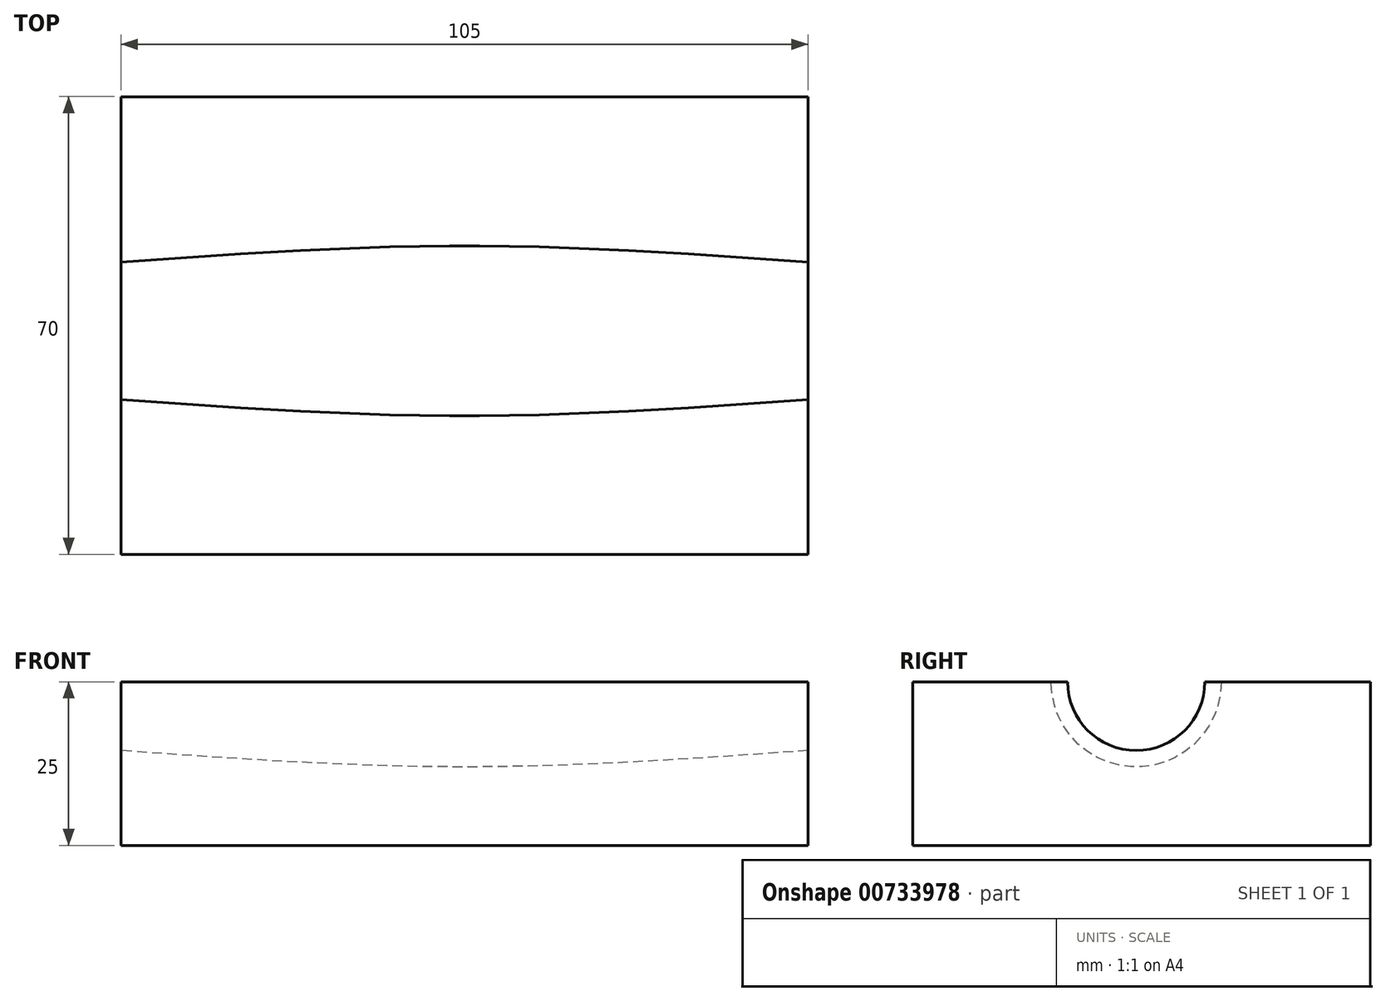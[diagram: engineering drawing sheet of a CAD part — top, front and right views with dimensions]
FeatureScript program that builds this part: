
annotation { "Feature Type Name" : "Feature", "Feature Type Description" : "" }
export const myFeature = defineFeature(function(context is Context, id is Id, definition is map)
    precondition{}
    {
        {
            var Q0;
            Q0=qCreatedBy(makeId("Front.planeOp"),FACE);
            var sketch = newSketch(context, id + "F0", { "sketchPlane" : qUnion([Q0])});
            skLineSegment(sketch, "E0", {"start": v(-90.68, 0) * mm, "end": v(100.6, 0) * mm, "construction": true});
            skLineSegment(sketch, "E1", {"start": v(-52.5, 0) * mm, "end": v(-52.5, 10.5) * mm});
            skLineSegment(sketch, "E2", {"start": v(52.5, 0) * mm, "end": v(52.5, 10.5) * mm});
            skLineSegment(sketch, "E3", {"start": v(-52.5, 0) * mm, "end": v(52.5, 0) * mm});
            skLineSegment(sketch, "E4", {"start": v(0, 0) * mm, "end": v(0, 13) * mm, "construction": true});
            skFitSpline(sketch, "E5", {"points": [v(-52.5, 10.5) * mm, v(0, 13) * mm, v(52.5, 10.5) * mm], "startDerivative": vector(105, 7.5) * mm, "endDerivative": vector(105, -7.5) * mm});
            skSolve(sketch);
        }
        {
            var Q0;
            Q0=qCreatedBy(makeId("Top.planeOp"),FACE);
            var sketch = newSketch(context, id + "F1", { "sketchPlane" : qUnion([Q0])});
            skLineSegment(sketch, "E6.bottom", {"start": v(-52.5, 35.82) * mm, "end": v(52.5, 35.82) * mm});
            skLineSegment(sketch, "E6.top", {"start": v(-52.5, -34.18) * mm, "end": v(52.5, -34.18) * mm});
            skLineSegment(sketch, "E6.left", {"start": v(-52.5, 35.82) * mm, "end": v(-52.5, -34.18) * mm});
            skLineSegment(sketch, "E6.right", {"start": v(52.5, 35.82) * mm, "end": v(52.5, -34.18) * mm});
            skSolve(sketch);
        }
        {
            var Q0;
            Q0 = qSketchRegion(id + "F1", true);
            extrude(context, id + "F2", {"entities" : qUnion([Q0]), "oppositeDirection" : true, "depth" : 25 * mm, "offsetDistance" : 25 * mm});
        }
        {
            var Q0;
            Q0=makeQuery(id+"F0.imprint","IMPRINT",FACE,{"disambiguationData":[TD([[makeQuery(id+"F0.imprint","IMPRINT",EDGE,{"derivedFrom":sQuery(id+"F0.wireOp",EDGE,"E1")}),-1.0]])]});
            var Q1;
            Q1=sQuery(id+"F0.wireOp",EDGE,"E0");
            revolve(context, id + "F3", {"operationType" : NewBodyOperationType.REMOVE, "surfaceOperationType" : NewSurfaceOperationType.NEW, "entities" : qUnion([Q0]), "axis" : qUnion([Q1]), "revolveType" : RevolveType.FULL, "oppositeDirection" : true});
        }
        {
            var Q0;
            Q0=makeQuery(id+"F2.opExtrude","SWEPT_BODY",BODY,{"disambiguationData":[OSD([sQuery(id+"F1.wireOp",EDGE,"E6.bottom"),sQuery(id+"F1.wireOp",EDGE,"E6.top"),sQuery(id+"F1.wireOp",EDGE,"E6.left"),sQuery(id+"F1.wireOp",EDGE,"E6.right")])]});
            var Q1;
            {var subQ0=sQuery(id+"F1.wireOp",EDGE,"E6.bottom");var subQ1=sQuery(id+"F1.wireOp",EDGE,"E6.right");Q1=makeQuery(id+"F3.boolean.opBoolean","SPLIT",EDGE,{"disambiguationData":[TD([makeQuery(id+"F2.opExtrude","SWEPT_FACE",FACE,{"disambiguationData":[OSD([subQ0])]})])],"derivedFrom":makeQuery(id+"F2.opExtrude","CAP_EDGE",EDGE,{"disambiguationData":[OSD([subQ1])],"isStart":true})});}
            transform(context, id + "F4", {"entities" : qUnion([Q0]), "transformType" : TransformType.ROTATION, "transformAxis" : qUnion([Q1]), "angle" : 180 * degree, "oppositeDirection" : true, "makeCopy" : true});
        }
        {
            var Q0;
            Q0=makeQuery(id+"F4.opPattern","COPY",BODY,{"derivedFrom":makeQuery(id+"F2.opExtrude","SWEPT_BODY",BODY,{"disambiguationData":[OSD([sQuery(id+"F1.wireOp",EDGE,"E6.bottom"),sQuery(id+"F1.wireOp",EDGE,"E6.top"),sQuery(id+"F1.wireOp",EDGE,"E6.left"),sQuery(id+"F1.wireOp",EDGE,"E6.right")])]}),"instanceName":"1"});
            deleteBodies(context, id + "F5", {"entities" : qUnion([Q0])});
        }
    });
